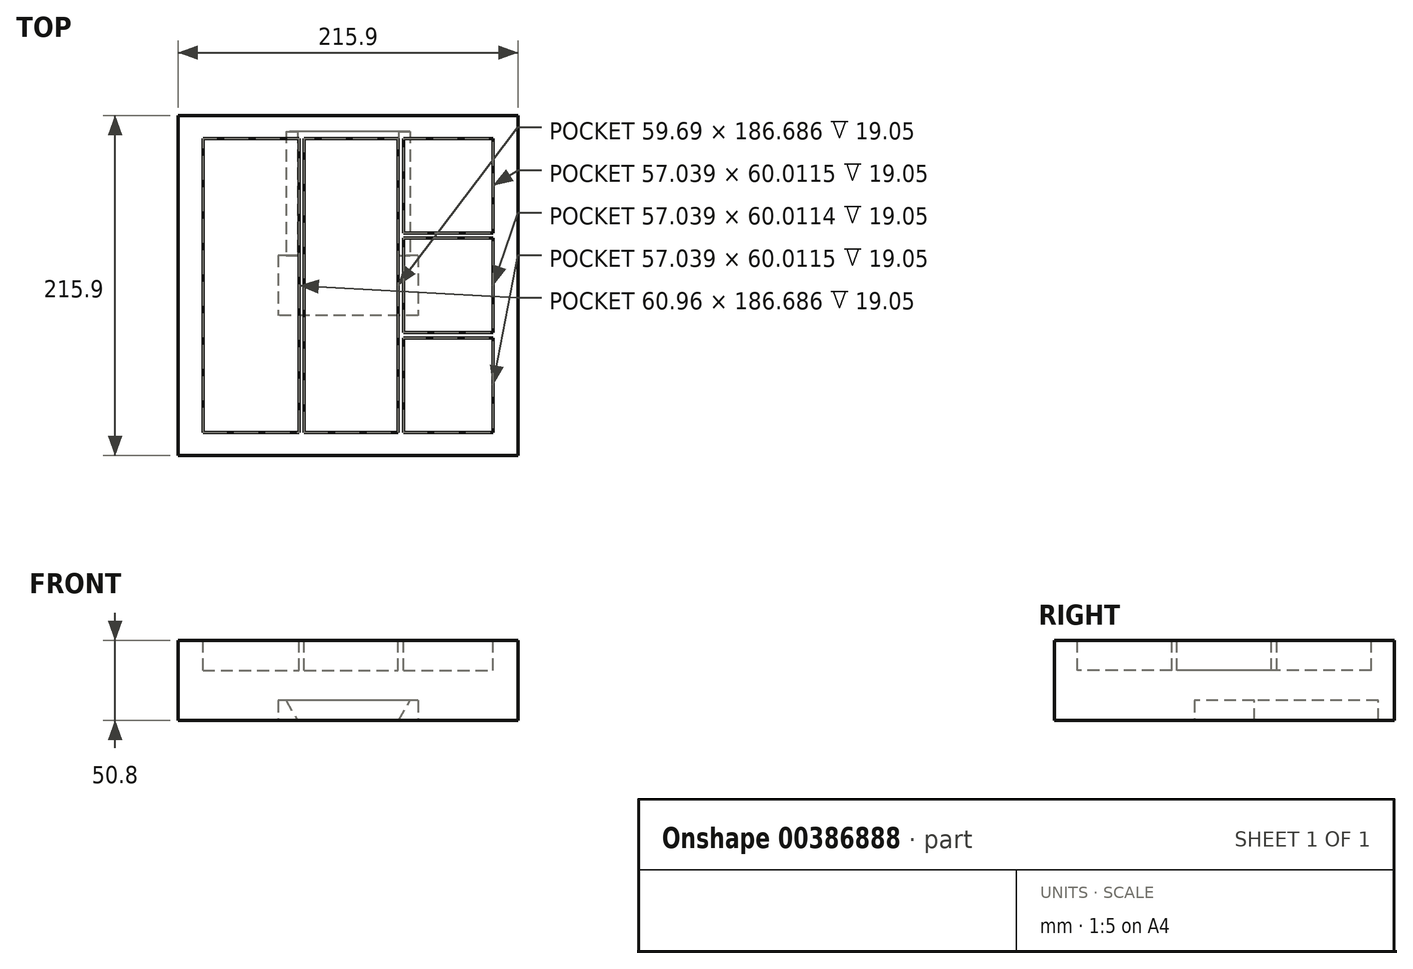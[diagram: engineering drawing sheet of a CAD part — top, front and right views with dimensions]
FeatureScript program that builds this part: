
annotation { "Feature Type Name" : "Feature", "Feature Type Description" : "" }
export const myFeature = defineFeature(function(context is Context, id is Id, definition is map)
    precondition{}
    {
        {
            var Q0;
            Q0=qCreatedBy(makeId("Top.planeOp"),FACE);
            var sketch = newSketch(context, id + "F0", { "sketchPlane" : qUnion([Q0])});
            skLineSegment(sketch, "E0.bottom", {"start": v(-107.95, 107.95) * mm, "end": v(107.95, 107.95) * mm});
            skLineSegment(sketch, "E0.top", {"start": v(-107.95, -107.95) * mm, "end": v(107.95, -107.95) * mm});
            skLineSegment(sketch, "E0.left", {"start": v(-107.95, 107.95) * mm, "end": v(-107.95, -107.95) * mm});
            skLineSegment(sketch, "E0.right", {"start": v(107.95, 107.95) * mm, "end": v(107.95, -107.95) * mm});
            skPoint(sketch, "E0.middle", {"position": v(0, 0) * mm});
            skSolve(sketch);
        }
        {
            var Q0;
            Q0=qSketchRegion(id+"F0",true);
            extrude(context, id + "F1", {"entities" : qUnion([Q0]), "depth" : 50.8 * mm});
        }
        {
            var Q0;
            Q0=makeQuery(id+"F1.opExtrude","CAP_FACE",FACE,{"disambiguationData":[OSD([sQuery(id+"F0.wireOp",EDGE,"E0.bottom"),sQuery(id+"F0.wireOp",EDGE,"E0.top"),sQuery(id+"F0.wireOp",EDGE,"E0.left"),sQuery(id+"F0.wireOp",EDGE,"E0.right")])],"isStart":false});
            var sketch = newSketch(context, id + "F2", { "sketchPlane" : qUnion([Q0])});
            skLineSegment(sketch, "E1.bottom", {"start": v(-92.17, 93.34) * mm, "end": v(-31.21, 93.34) * mm});
            skLineSegment(sketch, "E1.top", {"start": v(-92.17, -93.34) * mm, "end": v(-31.21, -93.34) * mm});
            skLineSegment(sketch, "E1.left", {"start": v(-92.17, 93.34) * mm, "end": v(-92.17, -93.34) * mm});
            skLineSegment(sketch, "E1.right", {"start": v(92.17, 33.33) * mm, "end": v(92.17, 30) * mm});
            skPoint(sketch, "E1.middle", {"position": v(0, 0) * mm});
            skLineSegment(sketch, "E2", {"start": v(-31.21, 93.34) * mm, "end": v(-31.21, -93.34) * mm});
            skLineSegment(sketch, "E3", {"start": v(-27.88, 93.34) * mm, "end": v(-27.88, -93.34) * mm});
            skLineSegment(sketch, "E4", {"start": v(31.8, 93.34) * mm, "end": v(31.8, -93.34) * mm});
            skLineSegment(sketch, "E5", {"start": v(35.13, 93.34) * mm, "end": v(35.13, -93.34) * mm});
            skLineSegment(sketch, "E6.trimOffspring", {"start": v(-27.88, 93.34) * mm, "end": v(31.8, 93.34) * mm});
            skLineSegment(sketch, "E7.trimOffspring", {"start": v(-27.88, -93.34) * mm, "end": v(31.8, -93.34) * mm});
            skLineSegment(sketch, "E8.trimOffspring", {"start": v(35.13, -93.34) * mm, "end": v(92.17, -93.34) * mm});
            skLineSegment(sketch, "E9.trimOffspring", {"start": v(35.13, 93.34) * mm, "end": v(92.17, 93.34) * mm});
            skLineSegment(sketch, "E10", {"start": v(92.17, 33.33) * mm, "end": v(35.13, 33.33) * mm});
            skLineSegment(sketch, "E11", {"start": v(92.17, -30) * mm, "end": v(35.13, -30) * mm});
            skLineSegment(sketch, "E12", {"start": v(92.17, -30) * mm, "end": v(92.17, -33.33) * mm});
            skLineSegment(sketch, "E13", {"start": v(92.17, -33.33) * mm, "end": v(35.13, -33.33) * mm});
            skLineSegment(sketch, "E14", {"start": v(35.13, -33.33) * mm, "end": v(35.13, -30) * mm});
            skLineSegment(sketch, "E15", {"start": v(92.17, 30) * mm, "end": v(35.13, 30) * mm});
            skLineSegment(sketch, "E16", {"start": v(31.8, -93.34) * mm, "end": v(35.13, -93.34) * mm});
            skLineSegment(sketch, "E17", {"start": v(-27.88, -93.34) * mm, "end": v(-31.21, -93.34) * mm});
            skLineSegment(sketch, "E18.trimOffspring", {"start": v(92.17, -30) * mm, "end": v(92.17, -93.34) * mm});
            skLineSegment(sketch, "E19", {"start": v(92.17, 93.34) * mm, "end": v(92.17, -30) * mm});
            skLineSegment(sketch, "E20", {"start": v(35.13, 33.33) * mm, "end": v(35.13, 93.34) * mm});
            skLineSegment(sketch, "E21", {"start": v(35.13, -30) * mm, "end": v(35.13, 30) * mm});
            skLineSegment(sketch, "E22", {"start": v(35.13, -93.34) * mm, "end": v(35.13, -33.33) * mm});
            skSolve(sketch);
        }
        {
            var Q0;
            Q0=makeQuery(id+"F2.imprint","IMPRINT",FACE,{"disambiguationData":[TD([[makeQuery(id+"F2.imprint","IMPRINT",EDGE,{"derivedFrom":sQuery(id+"F2.wireOp",EDGE,"E1.bottom")}),-1.0]])]});
            var Q1;
            Q1=makeQuery(id+"F2.imprint","IMPRINT",FACE,{"disambiguationData":[TD([[makeQuery(id+"F2.imprint","IMPRINT",EDGE,{"derivedFrom":sQuery(id+"F2.wireOp",EDGE,"E3")}),1.0]])]});
            var Q2;
            {var subQ0=sQuery(id+"F2.wireOp",EDGE,"E9.trimOffspring");Q2=makeQuery(id+"F2.imprint","IMPRINT",FACE,{"disambiguationData":[TD([[makeQuery(id+"F2.imprint","IMPRINT",EDGE,{"derivedFrom":subQ0}),-1.0]])]});}
            var Q3;
            {var subQ0=sQuery(id+"F2.wireOp",EDGE,"E11");Q3=makeQuery(id+"F2.imprint","IMPRINT",FACE,{"disambiguationData":[TD([[makeQuery(id+"F2.imprint","IMPRINT",EDGE,{"derivedFrom":subQ0}),-1.0]])]});}
            var Q4;
            {var subQ0=sQuery(id+"F2.wireOp",EDGE,"E8.trimOffspring");Q4=makeQuery(id+"F2.imprint","IMPRINT",FACE,{"disambiguationData":[TD([[makeQuery(id+"F2.imprint","IMPRINT",EDGE,{"derivedFrom":subQ0}),1.0]])]});}
            extrude(context, id + "F3", {"entities" : qUnion([Q0, Q1, Q2, Q3, Q4]), "operationType" : NewBodyOperationType.REMOVE, "oppositeDirection" : true, "depth" : 19.05 * mm});
        }
        {
            var Q0;
            Q0=makeQuery(id+"F1.opExtrude","CAP_FACE",FACE,{"disambiguationData":[OSD([sQuery(id+"F0.wireOp",EDGE,"E0.bottom"),sQuery(id+"F0.wireOp",EDGE,"E0.top"),sQuery(id+"F0.wireOp",EDGE,"E0.left"),sQuery(id+"F0.wireOp",EDGE,"E0.right")])],"isStart":true});
            var sketch = newSketch(context, id + "F4", { "sketchPlane" : qUnion([Q0])});
            skLineSegment(sketch, "E23.bottom", {"start": v(44.45, -19.05) * mm, "end": v(-44.45, -19.05) * mm});
            skLineSegment(sketch, "E23.top", {"start": v(44.45, 19.05) * mm, "end": v(-44.45, 19.05) * mm});
            skLineSegment(sketch, "E23.left", {"start": v(44.45, -19.05) * mm, "end": v(44.45, 19.05) * mm});
            skLineSegment(sketch, "E23.right", {"start": v(-44.45, -19.05) * mm, "end": v(-44.45, 19.05) * mm});
            skPoint(sketch, "E23.middle", {"position": v(0, 0) * mm});
            skSolve(sketch);
        }
        {
            var Q0;
            Q0=qSketchRegion(id+"F4",true);
            extrude(context, id + "F5", {"entities" : qUnion([Q0]), "operationType" : NewBodyOperationType.REMOVE, "oppositeDirection" : true, "depth" : 12.7 * mm});
        }
        {
            var Q0;
            Q0=makeQuery(id+"F5.boolean.opBoolean","COPY",FACE,{"derivedFrom":makeQuery(id+"F5.opExtrude","SWEPT_FACE",FACE,{"disambiguationData":[OSD([sQuery(id+"F4.wireOp",EDGE,"E23.bottom")])]})});
            var sketch = newSketch(context, id + "F6", { "sketchPlane" : qUnion([Q0])});
            skLineSegment(sketch, "E24", {"start": v(0, 0) * mm, "end": v(32.13, 0) * mm});
            skLineSegment(sketch, "E25", {"start": v(32.13, 0) * mm, "end": v(39.42, 12.7) * mm});
            skLineSegment(sketch, "E26", {"start": v(39.42, 12.7) * mm, "end": v(-39.42, 12.7) * mm});
            skLineSegment(sketch, "E27", {"start": v(-39.42, 12.7) * mm, "end": v(-32.13, 0) * mm});
            skLineSegment(sketch, "E28", {"start": v(-32.13, 0) * mm, "end": v(0, 0) * mm});
            skLineSegment(sketch, "E29", {"start": v(32.13, 0) * mm, "end": v(0, 0) * mm});
            skSolve(sketch);
        }
        {
            var Q0;
            Q0=qSketchRegion(id+"F6",true);
            extrude(context, id + "F7", {"entities" : qUnion([Q0]), "operationType" : NewBodyOperationType.REMOVE, "oppositeDirection" : true, "depth" : 78.74 * mm});
        }
    });
